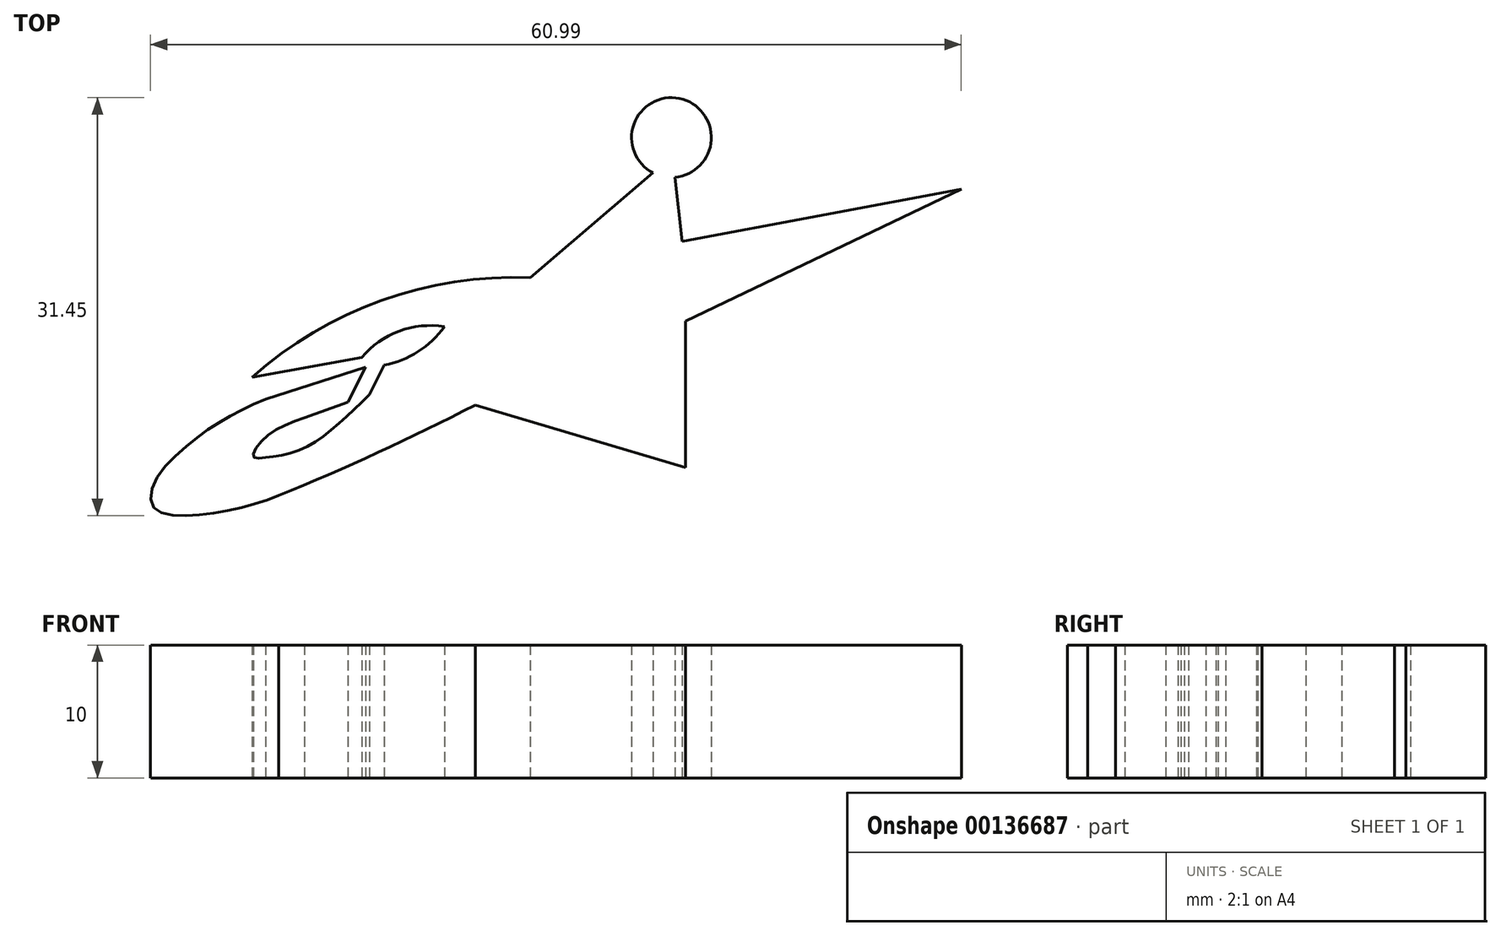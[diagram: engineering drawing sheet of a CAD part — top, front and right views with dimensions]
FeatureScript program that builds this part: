
annotation { "Feature Type Name" : "Feature", "Feature Type Description" : "" }
export const myFeature = defineFeature(function(context is Context, id is Id, definition is map)
    precondition{}
    {
        {
            var Q0;
            Q0=qCreatedBy(makeId("Top.planeOp"),FACE);
            var sketch = newSketch(context, id + "F0", { "sketchPlane" : qUnion([Q0])});
            skArc(sketch, "E0", {"start": v(-0.77, 4.46) * mm, "mid": v(-11.95, 2.72) * mm, "end": v(-21.7, -3.04) * mm});
            skLineSegment(sketch, "E1", {"start": v(-0.77, 4.46) * mm, "end": v(8.48, 12.34) * mm});
            skLineSegment(sketch, "E2", {"start": v(10.12, 12.01) * mm, "end": v(10.66, 7.17) * mm});
            skLineSegment(sketch, "E3", {"start": v(10.66, 7.17) * mm, "end": v(31.67, 11.13) * mm});
            skLineSegment(sketch, "E4", {"start": v(31.67, 11.13) * mm, "end": v(10.93, 1.18) * mm});
            skLineSegment(sketch, "E5", {"start": v(10.93, 1.18) * mm, "end": v(10.93, -9.84) * mm});
            skLineSegment(sketch, "E6", {"start": v(10.93, -9.84) * mm, "end": v(-4.9, -5.13) * mm});
            skLineSegment(sketch, "E7", {"start": v(-21.7, -3.04) * mm, "end": v(-13.44, -1.56) * mm});
            skArc(sketch, "E8", {"start": v(-7.22, 0.76) * mm, "mid": v(-10.64, 0.42) * mm, "end": v(-13.44, -1.56) * mm});
            skArc(sketch, "E9", {"start": v(10.12, 12.01) * mm, "mid": v(10.46, 17.94) * mm, "end": v(8.48, 12.34) * mm});
            skFitSpline(sketch, "E10", {"points": [v(-28.46, -11.18) * mm, v(-28.65, -11.44) * mm], "startDerivative": vector(-0.2, -0.26) * mm, "endDerivative": vector(-0.2, -0.26) * mm});
            skArc(sketch, "E11", {"start": v(-19.68, -11.94) * mm, "mid": v(-12.2, -8.7) * mm, "end": v(-4.9, -5.13) * mm});
            skFitSpline(sketch, "E12", {"points": [v(-20.68, -4.68) * mm, v(-23.7, -6.16) * mm, v(-26.53, -8.16) * mm, v(-29.06, -11) * mm, v(-29.06, -12.88) * mm, v(-26.75, -13.45) * mm, v(-22.94, -12.96) * mm, v(-19.68, -11.94) * mm], "startDerivative": vector(-20.61, -9.28) * mm, "endDerivative": vector(18.44, 7.87) * mm});
            skArc(sketch, "E13", {"start": v(-11.74, -2.14) * mm, "mid": v(-9.2, -1.12) * mm, "end": v(-7.22, 0.76) * mm});
            skFitSpline(sketch, "E14", {"points": [v(-12.85, -4.36) * mm, v(-15.6, -6.9) * mm, v(-18.26, -8.58) * mm, v(-20.7, -9.1) * mm, v(-21.58, -9.02) * mm, v(-20.77, -7.64) * mm, v(-17.76, -6.08) * mm], "startDerivative": vector(-13.12, -12.77) * mm, "endDerivative": vector(16.91, 6.3) * mm});
            skFitSpline(sketch, "E15", {"points": [v(-17.76, -6.08) * mm, v(-12.85, -4.36) * mm], "startDerivative": vector(4.9, 1.73) * mm, "endDerivative": vector(4.9, 1.73) * mm});
            skLineSegment(sketch, "E16", {"start": v(-13.16, -2.28) * mm, "end": v(-20.68, -4.68) * mm});
            skLineSegment(sketch, "E17", {"start": v(-13.16, -2.28) * mm, "end": v(-14.49, -4.93) * mm});
            skLineSegment(sketch, "E18", {"start": v(-12.85, -4.36) * mm, "end": v(-11.74, -2.14) * mm});
            skSolve(sketch);
        }
        {
            var Q0;
            Q0=makeQuery(id+"F0.imprint","IMPRINT",FACE,{"disambiguationData":[TD([[makeQuery(id+"F0.imprint","IMPRINT",EDGE,{"derivedFrom":sQuery(id+"F0.wireOp",EDGE,"E0")}),1.0]])]});
            extrude(context, id + "F1", {"entities" : qUnion([Q0]), "depth" : 10 * mm});
        }
    });
